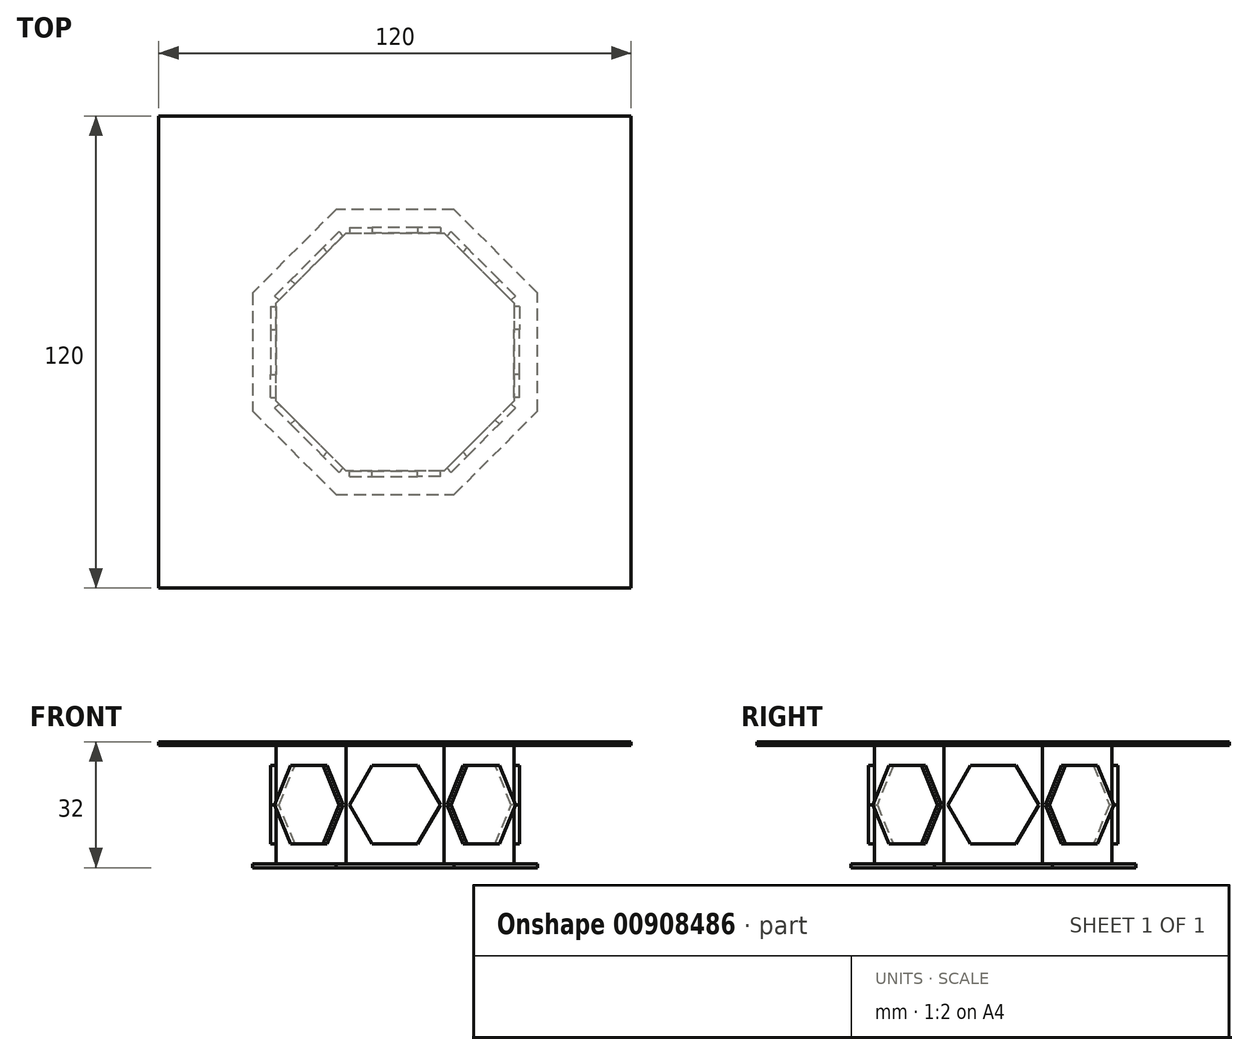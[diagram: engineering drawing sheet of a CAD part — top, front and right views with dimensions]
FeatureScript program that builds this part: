
annotation { "Feature Type Name" : "Feature", "Feature Type Description" : "" }
export const myFeature = defineFeature(function(context is Context, id is Id, definition is map)
    precondition{}
    {
        {
            var Q0;
            Q0=qCreatedBy(makeId("Front.planeOp"),FACE);
            var sketch = newSketch(context, id + "F0", { "sketchPlane" : qUnion([Q0])});
            skLineSegment(sketch, "E0", {"start": v(0, 52.03) * mm, "end": v(0, -45.25) * mm});
            skSolve(sketch);
        }
        {
            var Q0;
            Q0=qCreatedBy(makeId("Top.planeOp"),FACE);
            var sketch = newSketch(context, id + "F1", { "sketchPlane" : qUnion([Q0])});
            skCircle(sketch, "E1.cCircle", {"center": v(0, 0) * mm, "radius": 30.18 * mm, "construction": true});
            skLineSegment(sketch, "E1.0", {"start": v(30.18, -12.5) * mm, "end": v(12.5, -30.18) * mm});
            skLineSegment(sketch, "E1.1", {"start": v(12.5, -30.18) * mm, "end": v(-12.5, -30.18) * mm});
            skLineSegment(sketch, "E1.2", {"start": v(-12.5, -30.18) * mm, "end": v(-30.18, -12.5) * mm});
            skLineSegment(sketch, "E1.3", {"start": v(-30.18, -12.5) * mm, "end": v(-30.18, 12.5) * mm});
            skLineSegment(sketch, "E1.4", {"start": v(-30.18, 12.5) * mm, "end": v(-12.5, 30.18) * mm});
            skLineSegment(sketch, "E1.5", {"start": v(-12.5, 30.18) * mm, "end": v(12.5, 30.18) * mm});
            skLineSegment(sketch, "E1.6", {"start": v(12.5, 30.18) * mm, "end": v(30.18, 12.5) * mm});
            skLineSegment(sketch, "E1.7", {"start": v(30.18, 12.5) * mm, "end": v(30.18, -12.5) * mm});
            skPoint(sketch, "E1.0.midPoint", {"position": v(21.34, -21.34) * mm});
            skSolve(sketch);
        }
        {
            var Q0;
            Q0 = qSketchRegion(id + "F1", true);
            extrude(context, id + "F2", {"entities" : qUnion([Q0]), "endBound" : BoundingType.SYMMETRIC, "depth" : 30 * mm, "offsetDistance" : 25 * mm});
        }
        {
            var Q0;
            Q0=makeQuery(id+"F2.opExtrude","SWEPT_FACE",FACE,{"disambiguationData":[OSD([sQuery(id+"F1.wireOp",EDGE,"E1.1")])]});
            var sketch = newSketch(context, id + "F3", { "sketchPlane" : qUnion([Q0])});
            skCircle(sketch, "E2.cCircle", {"center": v(0, 0) * mm, "radius": 10 * mm, "construction": true});
            skLineSegment(sketch, "E2.0", {"start": v(11.55, 0) * mm, "end": v(5.77, -10) * mm});
            skLineSegment(sketch, "E2.1", {"start": v(5.77, -10) * mm, "end": v(-5.77, -10) * mm});
            skLineSegment(sketch, "E2.2", {"start": v(-5.77, -10) * mm, "end": v(-11.55, 0) * mm});
            skLineSegment(sketch, "E2.3", {"start": v(-11.55, 0) * mm, "end": v(-5.77, 10) * mm});
            skLineSegment(sketch, "E2.4", {"start": v(-5.77, 10) * mm, "end": v(5.77, 10) * mm});
            skLineSegment(sketch, "E2.5", {"start": v(5.77, 10) * mm, "end": v(11.55, 0) * mm});
            skPoint(sketch, "E2.0.midPoint", {"position": v(8.66, -5) * mm});
            skSolve(sketch);
        }
        {
            var Q0;
            Q0 = qSketchRegion(id + "F3", true);
            extrude(context, id + "F4", {"entities" : qUnion([Q0]), "depth" : 1.5 * mm, "offsetDistance" : 25 * mm});
        }
        {
            var Q0;
            Q0=makeQuery(id+"F4.opExtrude","SWEPT_BODY",BODY,{"disambiguationData":[OSD([sQuery(id+"F3.wireOp",EDGE,"E2.0"),sQuery(id+"F3.wireOp",EDGE,"E2.1"),sQuery(id+"F3.wireOp",EDGE,"E2.2"),sQuery(id+"F3.wireOp",EDGE,"E2.3"),sQuery(id+"F3.wireOp",EDGE,"E2.4"),sQuery(id+"F3.wireOp",EDGE,"E2.5")])]});
            var Q1;
            Q1=sQuery(id+"F0.wireOp",EDGE,"E0");
            circularPattern(context, id + "F5", {"entities" : qUnion([Q0]), "axis" : qUnion([Q1]), "angle" : 360 * degree, "instanceCount" : 8, "equalSpace" : true});
        }
        {
            var Q0;
            Q0=makeQuery(id+"F2.opExtrude","CAP_FACE",FACE,{"disambiguationData":[OSD([sQuery(id+"F1.wireOp",EDGE,"E1.0"),sQuery(id+"F1.wireOp",EDGE,"E1.1"),sQuery(id+"F1.wireOp",EDGE,"E1.2"),sQuery(id+"F1.wireOp",EDGE,"E1.3"),sQuery(id+"F1.wireOp",EDGE,"E1.4"),sQuery(id+"F1.wireOp",EDGE,"E1.5"),sQuery(id+"F1.wireOp",EDGE,"E1.6"),sQuery(id+"F1.wireOp",EDGE,"E1.7")])],"isStart":false});
            var sketch = newSketch(context, id + "F6", { "sketchPlane" : qUnion([Q0])});
            skLineSegment(sketch, "E3.bottom", {"start": v(60, 60) * mm, "end": v(-60, 60) * mm});
            skLineSegment(sketch, "E3.top", {"start": v(60, -60) * mm, "end": v(-60, -60) * mm});
            skLineSegment(sketch, "E3.left", {"start": v(60, 60) * mm, "end": v(60, -60) * mm});
            skLineSegment(sketch, "E3.right", {"start": v(-60, 60) * mm, "end": v(-60, -60) * mm});
            skPoint(sketch, "E3.middle", {"position": v(0, 0) * mm});
            skSolve(sketch);
        }
        {
            var Q0;
            Q0=makeQuery(id+"F6.imprint","IMPRINT",FACE,{"disambiguationData":[TD([[makeQuery(id+"F6.imprint","IMPRINT",EDGE,{"derivedFrom":makeQuery(id+"F2.opExtrude","CAP_EDGE",EDGE,{"disambiguationData":[OSD([sQuery(id+"F1.wireOp",EDGE,"E1.0")])],"isStart":false})}),-1.0]])]});
            var Q1;
            Q1=makeQuery(id+"F6.imprint","IMPRINT",FACE,{"disambiguationData":[TD([[makeQuery(id+"F6.imprint","IMPRINT",EDGE,{"derivedFrom":sQuery(id+"F6.wireOp",EDGE,"E3.bottom")}),1.0]])]});
            extrude(context, id + "F7", {"entities" : qUnion([Q0, Q1]), "depth" : 1 * mm, "offsetDistance" : 25 * mm});
        }
        {
            var Q0;
            Q0=makeQuery(id+"F2.opExtrude","CAP_FACE",FACE,{"disambiguationData":[OSD([sQuery(id+"F1.wireOp",EDGE,"E1.0"),sQuery(id+"F1.wireOp",EDGE,"E1.1"),sQuery(id+"F1.wireOp",EDGE,"E1.2"),sQuery(id+"F1.wireOp",EDGE,"E1.3"),sQuery(id+"F1.wireOp",EDGE,"E1.4"),sQuery(id+"F1.wireOp",EDGE,"E1.5"),sQuery(id+"F1.wireOp",EDGE,"E1.6"),sQuery(id+"F1.wireOp",EDGE,"E1.7")])],"isStart":true});
            var sketch = newSketch(context, id + "F8", { "sketchPlane" : qUnion([Q0])});
            skCircle(sketch, "E4.cCircle", {"center": v(0, 0) * mm, "radius": 36.21 * mm, "construction": true});
            skPoint(sketch, "E4.cCircle.perimeterSnap0", {"position": v(30.18, 0) * mm});
            skLineSegment(sketch, "E4.0", {"start": v(36.21, 15) * mm, "end": v(36.21, -15) * mm});
            skLineSegment(sketch, "E4.1", {"start": v(36.21, -15) * mm, "end": v(15, -36.21) * mm});
            skLineSegment(sketch, "E4.2", {"start": v(15, -36.21) * mm, "end": v(-15, -36.21) * mm});
            skLineSegment(sketch, "E4.3", {"start": v(-15, -36.21) * mm, "end": v(-36.21, -15) * mm});
            skLineSegment(sketch, "E4.4", {"start": v(-36.21, -15) * mm, "end": v(-36.21, 15) * mm});
            skLineSegment(sketch, "E4.5", {"start": v(-36.21, 15) * mm, "end": v(-15, 36.21) * mm});
            skLineSegment(sketch, "E4.6", {"start": v(-15, 36.21) * mm, "end": v(15, 36.21) * mm});
            skLineSegment(sketch, "E4.7", {"start": v(15, 36.21) * mm, "end": v(36.21, 15) * mm});
            skPoint(sketch, "E4.0.midPoint", {"position": v(36.21, 0) * mm});
            skPoint(sketch, "E4.0.midPoint.positionSnap0", {"position": v(30.18, 0) * mm});
            skSolve(sketch);
        }
        {
            var Q0;
            Q0 = qSketchRegion(id + "F8", true);
            extrude(context, id + "F9", {"entities" : qUnion([Q0]), "operationType" : NewBodyOperationType.ADD, "depth" : 1 * mm, "offsetDistance" : 25 * mm});
        }
    });
